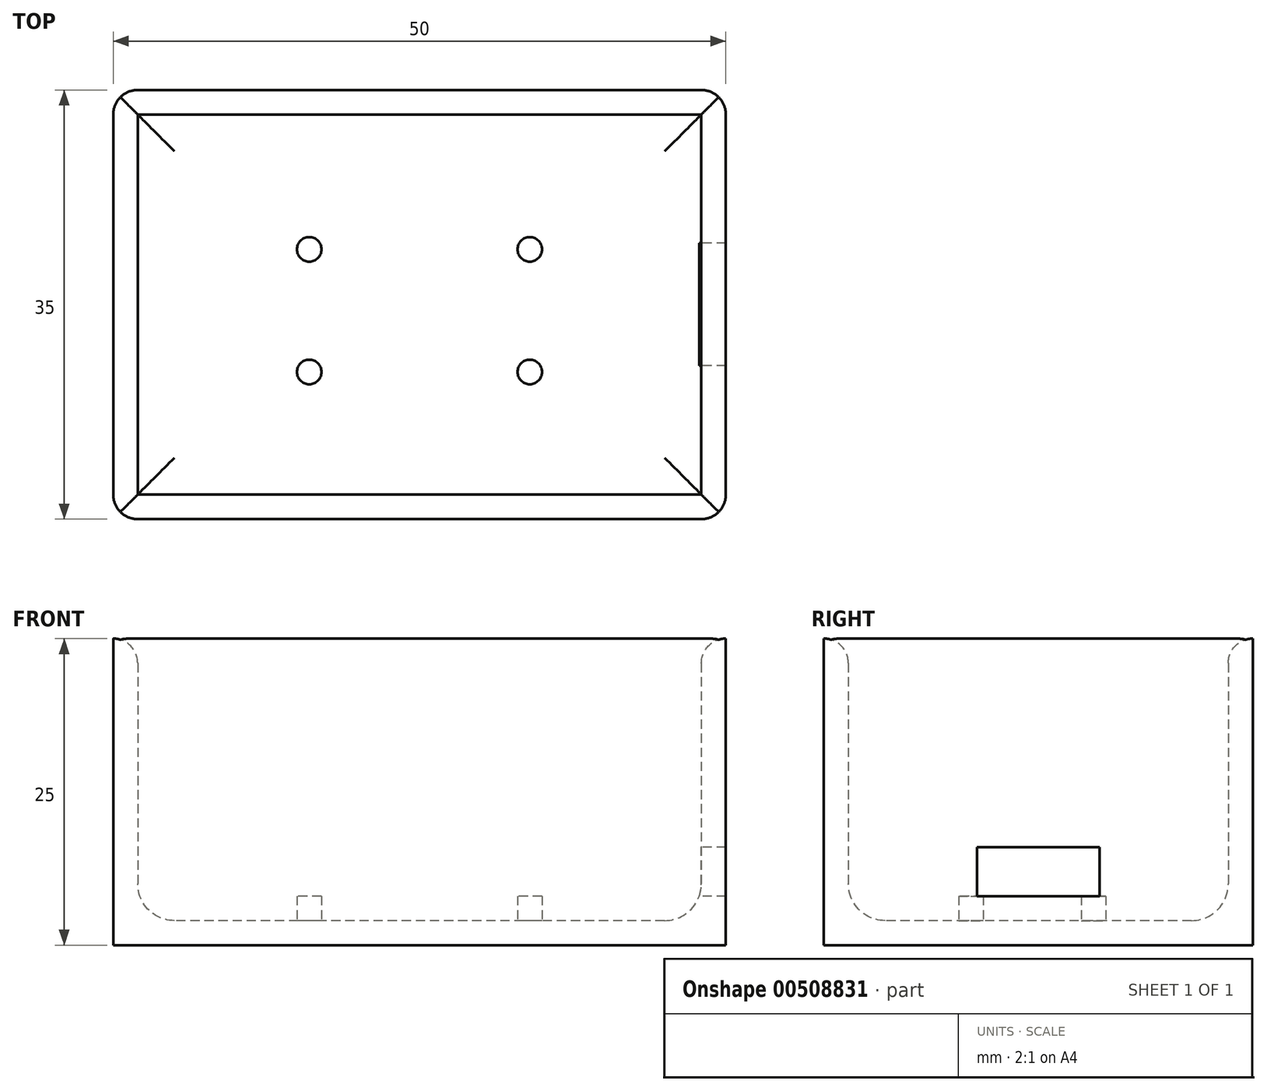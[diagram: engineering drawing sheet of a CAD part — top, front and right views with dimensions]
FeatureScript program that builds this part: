
annotation { "Feature Type Name" : "Feature", "Feature Type Description" : "" }
export const myFeature = defineFeature(function(context is Context, id is Id, definition is map)
    precondition{}
    {
        {
            var Q0;
            Q0=qCreatedBy(makeId("Top.planeOp"),FACE);
            var sketch = newSketch(context, id + "F0", { "sketchPlane" : qUnion([Q0])});
            skLineSegment(sketch, "E0.bottom", {"start": v(23, 17.5) * mm, "end": v(-23, 17.5) * mm});
            skLineSegment(sketch, "E0.top", {"start": v(23, -17.5) * mm, "end": v(-23, -17.5) * mm});
            skLineSegment(sketch, "E0.left", {"start": v(25, 15.5) * mm, "end": v(25, -15.5) * mm});
            skLineSegment(sketch, "E0.right", {"start": v(-25, 15.5) * mm, "end": v(-25, -15.5) * mm});
            skPoint(sketch, "E0.middle", {"position": v(0, 0) * mm});
            skPoint(sketch, "E1.visualSharp", {"position": v(-25, 17.5) * mm});
            skArc(sketch, "E1.filletArc", {"start": v(-23, 17.5) * mm, "mid": v(-24.41, 16.91) * mm, "end": v(-25, 15.5) * mm});
            skPoint(sketch, "E2.visualSharp", {"position": v(-25, -17.5) * mm});
            skArc(sketch, "E2.filletArc", {"start": v(-25, -15.5) * mm, "mid": v(-24.41, -16.91) * mm, "end": v(-23, -17.5) * mm});
            skPoint(sketch, "E3.visualSharp", {"position": v(25, 17.5) * mm});
            skArc(sketch, "E3.filletArc", {"start": v(25, 15.5) * mm, "mid": v(24.41, 16.91) * mm, "end": v(23, 17.5) * mm});
            skPoint(sketch, "E4.visualSharp", {"position": v(25, -17.5) * mm});
            skArc(sketch, "E4.filletArc", {"start": v(23, -17.5) * mm, "mid": v(24.41, -16.91) * mm, "end": v(25, -15.5) * mm});
            skPoint(sketch, "E5", {"position": v(-12.45, 6.5) * mm});
            skPoint(sketch, "E6", {"position": v(9.55, 6.5) * mm});
            skPoint(sketch, "E7", {"position": v(9.55, -3.5) * mm});
            skPoint(sketch, "E8", {"position": v(-12.45, -3.5) * mm});
            skSolve(sketch);
        }
        {
            var Q0;
            Q0=makeQuery(id+"F0.imprint","IMPRINT",FACE,{"disambiguationData":[TD([[makeQuery(id+"F0.imprint","IMPRINT",EDGE,{"derivedFrom":sQuery(id+"F0.wireOp",EDGE,"E0.bottom")}),1.0]])]});
            extrude(context, id + "F1", {"entities" : qUnion([Q0]), "depth" : 25 * mm});
        }
        {
            var Q0;
            Q0=makeQuery(id+"F1.opExtrude","CAP_FACE",FACE,{"disambiguationData":[OSD([sQuery(id+"F0.wireOp",EDGE,"E0.bottom"),sQuery(id+"F0.wireOp",EDGE,"E0.top"),sQuery(id+"F0.wireOp",EDGE,"E0.left"),sQuery(id+"F0.wireOp",EDGE,"E0.right"),sQuery(id+"F0.wireOp",EDGE,"E1.filletArc"),sQuery(id+"F0.wireOp",EDGE,"E2.filletArc"),sQuery(id+"F0.wireOp",EDGE,"E3.filletArc"),sQuery(id+"F0.wireOp",EDGE,"E4.filletArc")])],"isStart":false});
            shell(context, id + "F2", {"entities" : qUnion([Q0]), "thickness" : 2 * mm});
        }
        {
            var Q0;
            {var subQ0=sQuery(id+"F0.wireOp",EDGE,"E0.right");Q0=makeQuery(id+"F2.opShell","OFFSET_EDGE",EDGE,{"disambiguationData":[OSD([subQ0]),TDD([makeQuery(id+"F1.opExtrude","CAP_EDGE",EDGE,{"disambiguationData":[OSD([subQ0])],"isStart":false})])]});}
            var Q1;
            {var subQ0=sQuery(id+"F0.wireOp",EDGE,"E0.bottom");Q1=makeQuery(id+"F2.opShell","OFFSET_EDGE",EDGE,{"disambiguationData":[OSD([subQ0]),TDD([makeQuery(id+"F1.opExtrude","CAP_EDGE",EDGE,{"disambiguationData":[OSD([subQ0])],"isStart":false})])]});}
            var Q2;
            {var subQ0=sQuery(id+"F0.wireOp",EDGE,"E0.left");Q2=makeQuery(id+"F2.opShell","OFFSET_EDGE",EDGE,{"disambiguationData":[OSD([subQ0]),TDD([makeQuery(id+"F1.opExtrude","CAP_EDGE",EDGE,{"disambiguationData":[OSD([subQ0])],"isStart":false})])]});}
            var Q3;
            {var subQ0=sQuery(id+"F0.wireOp",EDGE,"E0.top");Q3=makeQuery(id+"F2.opShell","OFFSET_EDGE",EDGE,{"disambiguationData":[OSD([subQ0]),TDD([makeQuery(id+"F1.opExtrude","CAP_EDGE",EDGE,{"disambiguationData":[OSD([subQ0])],"isStart":false})])]});}
            fillet(context, id + "F3", {"entities" : qUnion([Q0, Q1, Q2, Q3]), "radius" : 2 * mm, "tangentPropagation" : true, "allowEdgeOverflow" : false});
        }
        {
            var Q0;
            {var subQ0=sQuery(id+"F0.wireOp",EDGE,"E0.bottom");Q0=makeQuery(id+"F2.opShell","OFFSET_EDGE",EDGE,{"disambiguationData":[OSD([subQ0]),TDD([makeQuery(id+"F1.opExtrude","CAP_EDGE",EDGE,{"disambiguationData":[OSD([subQ0])],"isStart":true})])]});}
            var Q1;
            {var subQ0=sQuery(id+"F0.wireOp",EDGE,"E0.left");Q1=makeQuery(id+"F2.opShell","OFFSET_EDGE",EDGE,{"disambiguationData":[OSD([subQ0]),TDD([makeQuery(id+"F1.opExtrude","CAP_EDGE",EDGE,{"disambiguationData":[OSD([subQ0])],"isStart":true})])]});}
            var Q2;
            {var subQ0=sQuery(id+"F0.wireOp",EDGE,"E0.top");Q2=makeQuery(id+"F2.opShell","OFFSET_EDGE",EDGE,{"disambiguationData":[OSD([subQ0]),TDD([makeQuery(id+"F1.opExtrude","CAP_EDGE",EDGE,{"disambiguationData":[OSD([subQ0])],"isStart":true})])]});}
            var Q3;
            {var subQ0=sQuery(id+"F0.wireOp",EDGE,"E0.right");Q3=makeQuery(id+"F2.opShell","OFFSET_EDGE",EDGE,{"disambiguationData":[OSD([subQ0]),TDD([makeQuery(id+"F1.opExtrude","CAP_EDGE",EDGE,{"disambiguationData":[OSD([subQ0])],"isStart":true})])]});}
            fillet(context, id + "F4", {"entities" : qUnion([Q0, Q1, Q2, Q3]), "radius" : 3 * mm, "tangentPropagation" : true, "allowEdgeOverflow" : false});
        }
        {
            var Q0;
            Q0=qCreatedBy(makeId("Top.planeOp"),FACE);
            var sketch = newSketch(context, id + "F5", { "sketchPlane" : qUnion([Q0])});
            skPoint(sketch, "E9", {"position": v(-9, 4.5) * mm});
            skPoint(sketch, "E10", {"position": v(-9, -5.5) * mm});
            skPoint(sketch, "E11", {"position": v(9, -5.5) * mm});
            skPoint(sketch, "E12", {"position": v(9, 4.5) * mm});
            skCircle(sketch, "E13", {"center": v(-9, 4.5) * mm, "radius": 1 * mm});
            skCircle(sketch, "E14", {"center": v(-9, -5.5) * mm, "radius": 1 * mm});
            skCircle(sketch, "E15", {"center": v(9, 4.5) * mm, "radius": 1 * mm});
            skCircle(sketch, "E16", {"center": v(9, -5.5) * mm, "radius": 1 * mm});
            skSolve(sketch);
        }
        {
            var Q0;
            Q0 = qSketchRegion(id + "F5", true);
            extrude(context, id + "F6", {"entities" : qUnion([Q0]), "operationType" : NewBodyOperationType.ADD, "depth" : 4 * mm});
        }
        {
            var Q0;
            Q0=qCreatedBy(makeId("Right.planeOp"),FACE);
            cPlane(context, id + "F7", {"entities" : qUnion([Q0]), "cplaneType" : CPlaneType.OFFSET, "offset" : 23.5 * mm, "width" : 150 * mm, "height" : 150 * mm});
        }
        {
            var Q0;
            Q0=qCreatedBy(id+"F7.planeOp",FACE);
            var sketch = newSketch(context, id + "F8", { "sketchPlane" : qUnion([Q0])});
            skPoint(sketch, "E17", {"position": v(0, 6) * mm});
            skLineSegment(sketch, "E18.bottom", {"start": v(-5, 8) * mm, "end": v(5, 8) * mm});
            skLineSegment(sketch, "E18.top", {"start": v(-5, 4) * mm, "end": v(5, 4) * mm});
            skLineSegment(sketch, "E18.left", {"start": v(-5, 8) * mm, "end": v(-5, 4) * mm});
            skLineSegment(sketch, "E18.right", {"start": v(5, 8) * mm, "end": v(5, 4) * mm});
            skSolve(sketch);
        }
        {
            var Q0;
            Q0=makeQuery(id+"F8.imprint","IMPRINT",FACE,{"disambiguationData":[TD([[makeQuery(id+"F8.imprint","IMPRINT",EDGE,{"derivedFrom":sQuery(id+"F8.wireOp",EDGE,"E18.bottom")}),-1.0]])]});
            extrude(context, id + "F9", {"entities" : qUnion([Q0]), "operationType" : NewBodyOperationType.REMOVE, "endBound" : BoundingType.SYMMETRIC, "depth" : 8 * mm});
        }
    });
